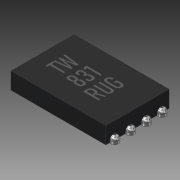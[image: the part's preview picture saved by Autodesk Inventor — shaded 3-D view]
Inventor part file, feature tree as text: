
AUTODESK INVENTOR PART (.ipt)
format: ipt  version: 2016 (Build 200138000, 138)  size: 467,968 bytes
history: native  units: mm
features: extrude x3, sketch x3, projected_geometry x2, plane x1, fillet x1
ambient origin geometry x8: Origin, YZ Plane, XZ Plane, XY Plane, X Axis, Y Axis, Z Axis, Center Point
bodies: Body1 (feature_tree)
feature tree (10):
  extrude  "Extrusion4"  Depth=3.0mm
  extrude  "Extrusion6"  Depth=0.25mm
  plane  "Work Plane1"
  extrude  "Extrusion5"  Depth=0.125mm
  fillet  "Fillet1"  Radius=0.45mm
  sketch  "Sketch10"  dims[d7=2.0mm d8=3.0mm]
  sketch  "Sketch11"  dims[d9=0.53mm d10=0.0mm d12=0.25mm]
  projected_geometry  "Projected Loop2"
  sketch  "Sketch12"  dims[d14=40.0mm d16=0.5mm d17=10.0mm d19=10.0mm d21=0.15mm d22=0.45mm d23=1.5mm d24=1.2mm d25=0.45mm d27=0.2mm d28=0.2mm d29=0.0mm d30=0.02mm d32=0.2mm d33=0.01mm d34=0.0mm d35=0.125mm]
  projected_geometry  "Projected Loop3"
